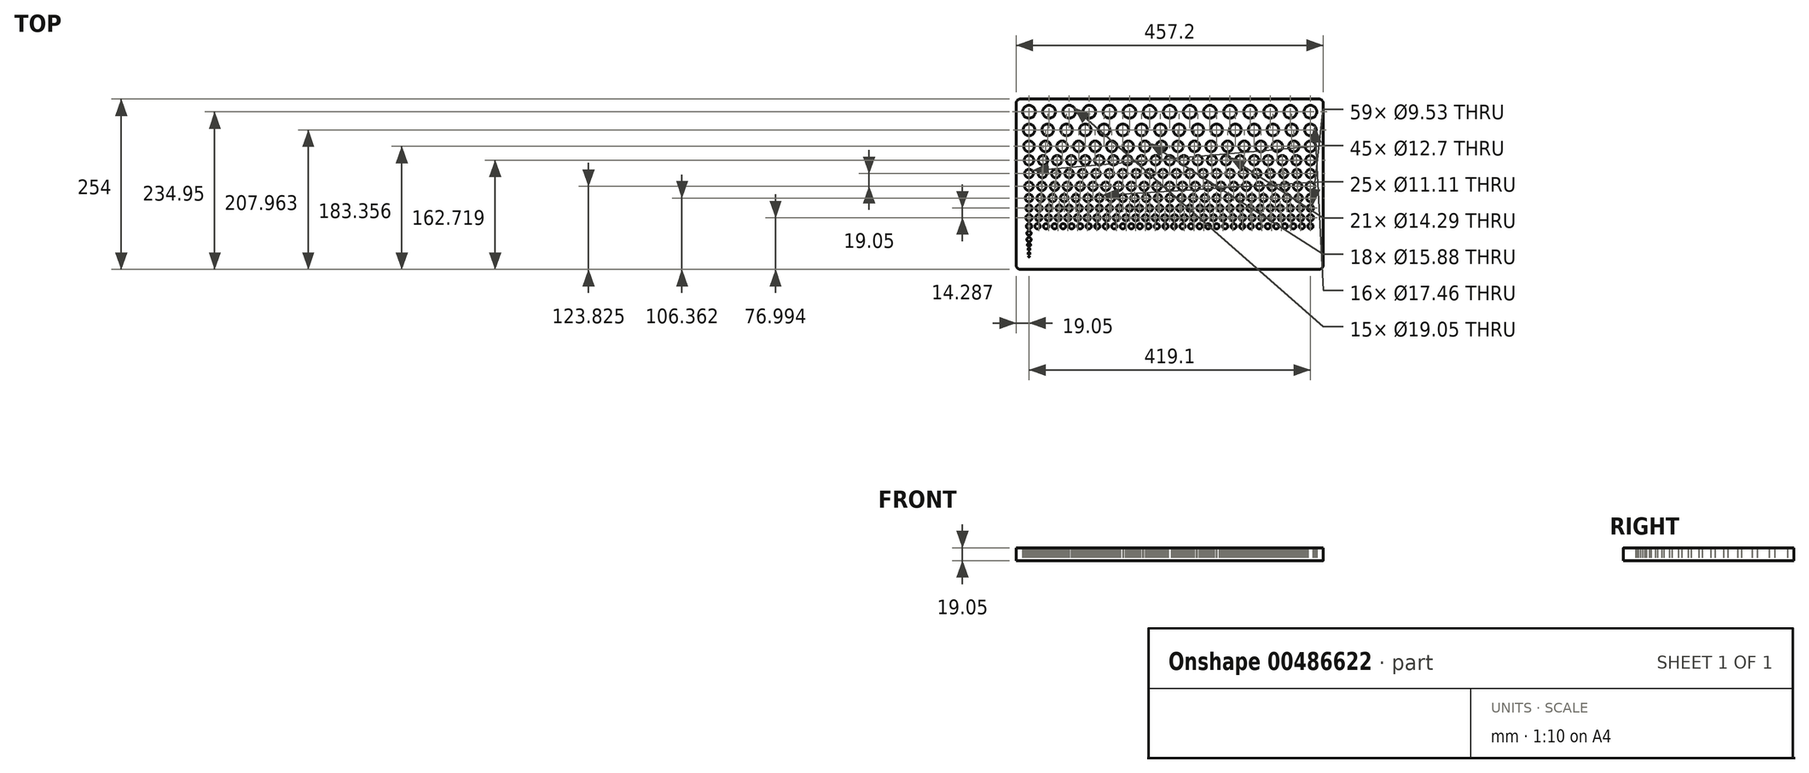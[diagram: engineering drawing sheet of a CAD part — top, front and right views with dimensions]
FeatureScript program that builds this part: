
annotation { "Feature Type Name" : "Feature", "Feature Type Description" : "" }
export const myFeature = defineFeature(function(context is Context, id is Id, definition is map)
    precondition{}
    {
        {
            var Q0;
            Q0=qCreatedBy(makeId("Top.planeOp"),FACE);
            var sketch = newSketch(context, id + "F0", { "sketchPlane" : qUnion([Q0])});
            skLineSegment(sketch, "E0.bottom", {"start": v(6.35, 0) * mm, "end": v(450.85, 0) * mm});
            skLineSegment(sketch, "E0.top", {"start": v(6.35, 254) * mm, "end": v(450.85, 254) * mm});
            skLineSegment(sketch, "E0.left", {"start": v(0, 6.35) * mm, "end": v(0, 247.65) * mm});
            skLineSegment(sketch, "E0.right", {"start": v(457.2, 6.35) * mm, "end": v(457.2, 247.65) * mm});
            skPoint(sketch, "E1.visualSharp", {"position": v(0, 254) * mm});
            skArc(sketch, "E1.filletArc", {"start": v(6.35, 254) * mm, "mid": v(1.86, 252.14) * mm, "end": v(0, 247.65) * mm});
            skPoint(sketch, "E2.visualSharp", {"position": v(457.2, 254) * mm});
            skArc(sketch, "E2.filletArc", {"start": v(457.2, 247.65) * mm, "mid": v(455.34, 252.14) * mm, "end": v(450.85, 254) * mm});
            skPoint(sketch, "E3.visualSharp", {"position": v(457.2, 0) * mm});
            skArc(sketch, "E3.filletArc", {"start": v(450.85, 0) * mm, "mid": v(455.34, 1.86) * mm, "end": v(457.2, 6.35) * mm});
            skPoint(sketch, "E4.visualSharp", {"position": v(0, 0) * mm});
            skArc(sketch, "E4.filletArc", {"start": v(0, 6.35) * mm, "mid": v(1.86, 1.86) * mm, "end": v(6.35, 0) * mm});
            skLineSegment(sketch, "E5", {"start": v(19.05, 234.95) * mm, "end": v(438.15, 234.95) * mm, "construction": true});
            skPoint(sketch, "E6", {"position": v(19.05, 234.95) * mm});
            skCircle(sketch, "E7", {"center": v(19.05, 234.95) * mm, "radius": 9.53 * mm});
            skLineSegment(sketch, "E8", {"start": v(19.05, 234.95) * mm, "end": v(19.05, 19.05) * mm, "construction": true});
            skCircle(sketch, "E9", {"center": v(19.05, 207.96) * mm, "radius": 8.73 * mm});
            skCircle(sketch, "E10.1.0.0", {"center": v(48.99, 234.95) * mm, "radius": 9.53 * mm});
            skCircle(sketch, "E10.2.0.0", {"center": v(78.92, 234.95) * mm, "radius": 9.53 * mm});
            skCircle(sketch, "E10.3.0.0", {"center": v(108.86, 234.95) * mm, "radius": 9.53 * mm});
            skCircle(sketch, "E10.4.0.0", {"center": v(138.8, 234.95) * mm, "radius": 9.53 * mm});
            skCircle(sketch, "E10.5.0.0", {"center": v(168.73, 234.95) * mm, "radius": 9.53 * mm});
            skCircle(sketch, "E10.6.0.0", {"center": v(198.66, 234.95) * mm, "radius": 9.53 * mm});
            skCircle(sketch, "E10.7.0.0", {"center": v(228.6, 234.95) * mm, "radius": 9.53 * mm});
            skCircle(sketch, "E10.8.0.0", {"center": v(258.54, 234.95) * mm, "radius": 9.53 * mm});
            skCircle(sketch, "E10.9.0.0", {"center": v(288.47, 234.95) * mm, "radius": 9.53 * mm});
            skCircle(sketch, "E10.10.0.0", {"center": v(318.4, 234.95) * mm, "radius": 9.53 * mm});
            skCircle(sketch, "E10.11.0.0", {"center": v(348.34, 234.95) * mm, "radius": 9.53 * mm});
            skCircle(sketch, "E10.12.0.0", {"center": v(378.28, 234.95) * mm, "radius": 9.53 * mm});
            skCircle(sketch, "E10.13.0.0", {"center": v(408.21, 234.95) * mm, "radius": 9.53 * mm});
            skCircle(sketch, "E10.14.0.0", {"center": v(438.15, 234.95) * mm, "radius": 9.53 * mm});
            skLineSegment(sketch, "E10.direction1", {"start": v(19.05, 234.95) * mm, "end": v(48.99, 234.95) * mm, "construction": true});
            skCircle(sketch, "E11", {"center": v(19.05, 183.36) * mm, "radius": 7.94 * mm});
            skCircle(sketch, "E12", {"center": v(19.05, 162.72) * mm, "radius": 7.14 * mm});
            skCircle(sketch, "E13", {"center": v(19.05, 142.88) * mm, "radius": 6.35 * mm});
            skCircle(sketch, "E14", {"center": v(19.05, 123.83) * mm, "radius": 6.35 * mm});
            skCircle(sketch, "E15", {"center": v(19.05, 106.36) * mm, "radius": 5.56 * mm});
            skCircle(sketch, "E16", {"center": v(19.05, 91.28) * mm, "radius": 4.76 * mm});
            skCircle(sketch, "E17", {"center": v(19.05, 77) * mm, "radius": 4.76 * mm});
            skCircle(sketch, "E18", {"center": v(19.05, 64.3) * mm, "radius": 3.97 * mm});
            skCircle(sketch, "E19", {"center": v(19.05, 53.97) * mm, "radius": 3.18 * mm});
            skCircle(sketch, "E20", {"center": v(19.05, 44.45) * mm, "radius": 3.18 * mm});
            skCircle(sketch, "E21", {"center": v(19.05, 36.51) * mm, "radius": 2.38 * mm});
            skCircle(sketch, "E22", {"center": v(19.05, 30.16) * mm, "radius": 1.59 * mm});
            skCircle(sketch, "E23", {"center": v(19.05, 23.81) * mm, "radius": 1.59 * mm});
            skCircle(sketch, "E24", {"center": v(19.05, 19.05) * mm, "radius": 0.8 * mm});
            skCircle(sketch, "E25.1.0.0", {"center": v(47, 207.96) * mm, "radius": 8.73 * mm});
            skCircle(sketch, "E25.2.0.0", {"center": v(74.93, 207.96) * mm, "radius": 8.73 * mm});
            skCircle(sketch, "E25.3.0.0", {"center": v(102.87, 207.96) * mm, "radius": 8.73 * mm});
            skCircle(sketch, "E25.4.0.0", {"center": v(130.81, 207.96) * mm, "radius": 8.73 * mm});
            skCircle(sketch, "E25.5.0.0", {"center": v(158.75, 207.96) * mm, "radius": 8.73 * mm});
            skCircle(sketch, "E25.6.0.0", {"center": v(186.7, 207.96) * mm, "radius": 8.73 * mm});
            skCircle(sketch, "E25.7.0.0", {"center": v(214.63, 207.96) * mm, "radius": 8.73 * mm});
            skCircle(sketch, "E25.8.0.0", {"center": v(242.57, 207.96) * mm, "radius": 8.73 * mm});
            skCircle(sketch, "E25.9.0.0", {"center": v(270.51, 207.96) * mm, "radius": 8.73 * mm});
            skCircle(sketch, "E25.10.0.0", {"center": v(298.45, 207.96) * mm, "radius": 8.73 * mm});
            skCircle(sketch, "E25.11.0.0", {"center": v(326.4, 207.96) * mm, "radius": 8.73 * mm});
            skCircle(sketch, "E25.12.0.0", {"center": v(354.33, 207.96) * mm, "radius": 8.73 * mm});
            skCircle(sketch, "E25.13.0.0", {"center": v(382.27, 207.96) * mm, "radius": 8.73 * mm});
            skCircle(sketch, "E25.14.0.0", {"center": v(410.21, 207.96) * mm, "radius": 8.73 * mm});
            skCircle(sketch, "E25.15.0.0", {"center": v(438.15, 207.96) * mm, "radius": 8.73 * mm});
            skLineSegment(sketch, "E25.direction1", {"start": v(19.05, 207.96) * mm, "end": v(47, 207.96) * mm, "construction": true});
            skCircle(sketch, "E26.1.0.0", {"center": v(43.7, 183.36) * mm, "radius": 7.94 * mm});
            skCircle(sketch, "E26.2.0.0", {"center": v(68.36, 183.36) * mm, "radius": 7.94 * mm});
            skCircle(sketch, "E26.3.0.0", {"center": v(93, 183.36) * mm, "radius": 7.94 * mm});
            skCircle(sketch, "E26.4.0.0", {"center": v(117.66, 183.36) * mm, "radius": 7.94 * mm});
            skCircle(sketch, "E26.5.0.0", {"center": v(142.31, 183.36) * mm, "radius": 7.94 * mm});
            skCircle(sketch, "E26.6.0.0", {"center": v(166.97, 183.36) * mm, "radius": 7.94 * mm});
            skCircle(sketch, "E26.7.0.0", {"center": v(191.62, 183.36) * mm, "radius": 7.94 * mm});
            skCircle(sketch, "E26.8.0.0", {"center": v(216.27, 183.36) * mm, "radius": 7.94 * mm});
            skCircle(sketch, "E26.9.0.0", {"center": v(240.93, 183.36) * mm, "radius": 7.94 * mm});
            skCircle(sketch, "E26.10.0.0", {"center": v(265.58, 183.36) * mm, "radius": 7.94 * mm});
            skCircle(sketch, "E26.11.0.0", {"center": v(290.23, 183.36) * mm, "radius": 7.94 * mm});
            skCircle(sketch, "E26.12.0.0", {"center": v(314.89, 183.36) * mm, "radius": 7.94 * mm});
            skCircle(sketch, "E26.13.0.0", {"center": v(339.54, 183.36) * mm, "radius": 7.94 * mm});
            skCircle(sketch, "E26.14.0.0", {"center": v(364.2, 183.36) * mm, "radius": 7.94 * mm});
            skCircle(sketch, "E26.15.0.0", {"center": v(388.84, 183.36) * mm, "radius": 7.94 * mm});
            skCircle(sketch, "E26.16.0.0", {"center": v(413.5, 183.36) * mm, "radius": 7.94 * mm});
            skCircle(sketch, "E26.17.0.0", {"center": v(438.15, 183.36) * mm, "radius": 7.94 * mm});
            skLineSegment(sketch, "E26.direction1", {"start": v(19.05, 183.36) * mm, "end": v(43.7, 183.36) * mm, "construction": true});
            skCircle(sketch, "E27.1.0.0", {"center": v(40, 162.72) * mm, "radius": 7.14 * mm});
            skCircle(sketch, "E27.2.0.0", {"center": v(60.96, 162.72) * mm, "radius": 7.14 * mm});
            skCircle(sketch, "E27.3.0.0", {"center": v(81.92, 162.72) * mm, "radius": 7.14 * mm});
            skCircle(sketch, "E27.4.0.0", {"center": v(102.87, 162.72) * mm, "radius": 7.14 * mm});
            skCircle(sketch, "E27.5.0.0", {"center": v(123.83, 162.72) * mm, "radius": 7.14 * mm});
            skCircle(sketch, "E27.6.0.0", {"center": v(144.78, 162.72) * mm, "radius": 7.14 * mm});
            skCircle(sketch, "E27.7.0.0", {"center": v(165.74, 162.72) * mm, "radius": 7.14 * mm});
            skCircle(sketch, "E27.8.0.0", {"center": v(186.7, 162.72) * mm, "radius": 7.14 * mm});
            skCircle(sketch, "E27.9.0.0", {"center": v(207.65, 162.72) * mm, "radius": 7.14 * mm});
            skCircle(sketch, "E27.10.0.0", {"center": v(228.6, 162.72) * mm, "radius": 7.14 * mm});
            skCircle(sketch, "E27.11.0.0", {"center": v(249.56, 162.72) * mm, "radius": 7.14 * mm});
            skCircle(sketch, "E27.12.0.0", {"center": v(270.51, 162.72) * mm, "radius": 7.14 * mm});
            skCircle(sketch, "E27.13.0.0", {"center": v(291.47, 162.72) * mm, "radius": 7.14 * mm});
            skCircle(sketch, "E27.14.0.0", {"center": v(312.42, 162.72) * mm, "radius": 7.14 * mm});
            skCircle(sketch, "E27.15.0.0", {"center": v(333.38, 162.72) * mm, "radius": 7.14 * mm});
            skCircle(sketch, "E27.16.0.0", {"center": v(354.33, 162.72) * mm, "radius": 7.14 * mm});
            skCircle(sketch, "E27.17.0.0", {"center": v(375.29, 162.72) * mm, "radius": 7.14 * mm});
            skCircle(sketch, "E27.18.0.0", {"center": v(396.24, 162.72) * mm, "radius": 7.14 * mm});
            skCircle(sketch, "E27.19.0.0", {"center": v(417.2, 162.72) * mm, "radius": 7.14 * mm});
            skLineSegment(sketch, "E27.direction1", {"start": v(19.05, 162.72) * mm, "end": v(40, 162.72) * mm, "construction": true});
            skCircle(sketch, "E28.0.20.0", {"center": v(438.15, 162.72) * mm, "radius": 7.14 * mm});
            skCircle(sketch, "E29.1.0.0", {"center": v(39, 142.88) * mm, "radius": 6.35 * mm});
            skCircle(sketch, "E29.2.0.0", {"center": v(58.96, 142.88) * mm, "radius": 6.35 * mm});
            skCircle(sketch, "E29.3.0.0", {"center": v(78.92, 142.88) * mm, "radius": 6.35 * mm});
            skCircle(sketch, "E29.4.0.0", {"center": v(98.88, 142.88) * mm, "radius": 6.35 * mm});
            skCircle(sketch, "E29.5.0.0", {"center": v(118.84, 142.88) * mm, "radius": 6.35 * mm});
            skCircle(sketch, "E29.6.0.0", {"center": v(138.8, 142.88) * mm, "radius": 6.35 * mm});
            skCircle(sketch, "E29.7.0.0", {"center": v(158.75, 142.88) * mm, "radius": 6.35 * mm});
            skCircle(sketch, "E29.8.0.0", {"center": v(178.7, 142.88) * mm, "radius": 6.35 * mm});
            skCircle(sketch, "E29.9.0.0", {"center": v(198.66, 142.88) * mm, "radius": 6.35 * mm});
            skCircle(sketch, "E29.10.0.0", {"center": v(218.62, 142.88) * mm, "radius": 6.35 * mm});
            skCircle(sketch, "E29.11.0.0", {"center": v(238.58, 142.88) * mm, "radius": 6.35 * mm});
            skCircle(sketch, "E29.12.0.0", {"center": v(258.54, 142.88) * mm, "radius": 6.35 * mm});
            skCircle(sketch, "E29.13.0.0", {"center": v(278.5, 142.88) * mm, "radius": 6.35 * mm});
            skCircle(sketch, "E29.14.0.0", {"center": v(298.45, 142.88) * mm, "radius": 6.35 * mm});
            skCircle(sketch, "E29.15.0.0", {"center": v(318.4, 142.88) * mm, "radius": 6.35 * mm});
            skCircle(sketch, "E29.16.0.0", {"center": v(338.36, 142.88) * mm, "radius": 6.35 * mm});
            skCircle(sketch, "E29.17.0.0", {"center": v(358.32, 142.88) * mm, "radius": 6.35 * mm});
            skCircle(sketch, "E29.18.0.0", {"center": v(378.28, 142.88) * mm, "radius": 6.35 * mm});
            skCircle(sketch, "E29.19.0.0", {"center": v(398.24, 142.88) * mm, "radius": 6.35 * mm});
            skCircle(sketch, "E29.20.0.0", {"center": v(418.2, 142.88) * mm, "radius": 6.35 * mm});
            skCircle(sketch, "E29.21.0.0", {"center": v(438.15, 142.88) * mm, "radius": 6.35 * mm});
            skLineSegment(sketch, "E29.direction1", {"start": v(19.05, 142.88) * mm, "end": v(39, 142.88) * mm, "construction": true});
            skCircle(sketch, "E30.1.0.0", {"center": v(38.1, 123.83) * mm, "radius": 6.35 * mm});
            skCircle(sketch, "E30.2.0.0", {"center": v(57.15, 123.83) * mm, "radius": 6.35 * mm});
            skLineSegment(sketch, "E30.direction1", {"start": v(19.05, 123.83) * mm, "end": v(38.1, 123.83) * mm, "construction": true});
            skCircle(sketch, "E31.0.3.0", {"center": v(76.2, 123.83) * mm, "radius": 6.35 * mm});
            skCircle(sketch, "E31.0.4.0", {"center": v(95.25, 123.83) * mm, "radius": 6.35 * mm});
            skCircle(sketch, "E31.0.5.0", {"center": v(114.3, 123.83) * mm, "radius": 6.35 * mm});
            skCircle(sketch, "E31.0.6.0", {"center": v(133.35, 123.83) * mm, "radius": 6.35 * mm});
            skCircle(sketch, "E31.0.7.0", {"center": v(152.4, 123.83) * mm, "radius": 6.35 * mm});
            skCircle(sketch, "E31.0.8.0", {"center": v(171.45, 123.83) * mm, "radius": 6.35 * mm});
            skCircle(sketch, "E31.0.9.0", {"center": v(190.5, 123.83) * mm, "radius": 6.35 * mm});
            skCircle(sketch, "E31.0.10.0", {"center": v(209.55, 123.83) * mm, "radius": 6.35 * mm});
            skCircle(sketch, "E31.0.11.0", {"center": v(228.6, 123.83) * mm, "radius": 6.35 * mm});
            skCircle(sketch, "E31.0.12.0", {"center": v(247.65, 123.83) * mm, "radius": 6.35 * mm});
            skCircle(sketch, "E31.0.13.0", {"center": v(266.7, 123.83) * mm, "radius": 6.35 * mm});
            skCircle(sketch, "E31.0.14.0", {"center": v(285.75, 123.83) * mm, "radius": 6.35 * mm});
            skCircle(sketch, "E31.0.15.0", {"center": v(304.8, 123.83) * mm, "radius": 6.35 * mm});
            skCircle(sketch, "E31.0.16.0", {"center": v(323.85, 123.83) * mm, "radius": 6.35 * mm});
            skCircle(sketch, "E31.0.17.0", {"center": v(342.9, 123.83) * mm, "radius": 6.35 * mm});
            skCircle(sketch, "E31.0.18.0", {"center": v(361.95, 123.83) * mm, "radius": 6.35 * mm});
            skCircle(sketch, "E31.0.19.0", {"center": v(381, 123.83) * mm, "radius": 6.35 * mm});
            skCircle(sketch, "E31.0.20.0", {"center": v(400.05, 123.83) * mm, "radius": 6.35 * mm});
            skCircle(sketch, "E31.0.21.0", {"center": v(419.1, 123.83) * mm, "radius": 6.35 * mm});
            skCircle(sketch, "E31.0.22.0", {"center": v(438.15, 123.83) * mm, "radius": 6.35 * mm});
            skCircle(sketch, "E32.1.0.0", {"center": v(36.51, 106.36) * mm, "radius": 5.56 * mm});
            skCircle(sketch, "E32.2.0.0", {"center": v(53.98, 106.36) * mm, "radius": 5.56 * mm});
            skCircle(sketch, "E32.3.0.0", {"center": v(71.44, 106.36) * mm, "radius": 5.56 * mm});
            skCircle(sketch, "E32.4.0.0", {"center": v(88.9, 106.36) * mm, "radius": 5.56 * mm});
            skCircle(sketch, "E32.5.0.0", {"center": v(106.36, 106.36) * mm, "radius": 5.56 * mm});
            skCircle(sketch, "E32.6.0.0", {"center": v(123.83, 106.36) * mm, "radius": 5.56 * mm});
            skCircle(sketch, "E32.7.0.0", {"center": v(141.29, 106.36) * mm, "radius": 5.56 * mm});
            skCircle(sketch, "E32.8.0.0", {"center": v(158.75, 106.36) * mm, "radius": 5.56 * mm});
            skCircle(sketch, "E32.9.0.0", {"center": v(176.21, 106.36) * mm, "radius": 5.56 * mm});
            skCircle(sketch, "E32.10.0.0", {"center": v(193.68, 106.36) * mm, "radius": 5.56 * mm});
            skCircle(sketch, "E32.11.0.0", {"center": v(211.14, 106.36) * mm, "radius": 5.56 * mm});
            skCircle(sketch, "E32.12.0.0", {"center": v(228.6, 106.36) * mm, "radius": 5.56 * mm});
            skCircle(sketch, "E32.13.0.0", {"center": v(246.06, 106.36) * mm, "radius": 5.56 * mm});
            skCircle(sketch, "E32.14.0.0", {"center": v(263.53, 106.36) * mm, "radius": 5.56 * mm});
            skCircle(sketch, "E32.15.0.0", {"center": v(280.99, 106.36) * mm, "radius": 5.56 * mm});
            skCircle(sketch, "E32.16.0.0", {"center": v(298.45, 106.36) * mm, "radius": 5.56 * mm});
            skCircle(sketch, "E32.17.0.0", {"center": v(315.91, 106.36) * mm, "radius": 5.56 * mm});
            skCircle(sketch, "E32.18.0.0", {"center": v(333.38, 106.36) * mm, "radius": 5.56 * mm});
            skCircle(sketch, "E32.19.0.0", {"center": v(350.84, 106.36) * mm, "radius": 5.56 * mm});
            skCircle(sketch, "E32.20.0.0", {"center": v(368.3, 106.36) * mm, "radius": 5.56 * mm});
            skCircle(sketch, "E32.21.0.0", {"center": v(385.76, 106.36) * mm, "radius": 5.56 * mm});
            skCircle(sketch, "E32.22.0.0", {"center": v(403.23, 106.36) * mm, "radius": 5.56 * mm});
            skCircle(sketch, "E32.23.0.0", {"center": v(420.69, 106.36) * mm, "radius": 5.56 * mm});
            skCircle(sketch, "E32.24.0.0", {"center": v(438.15, 106.36) * mm, "radius": 5.56 * mm});
            skLineSegment(sketch, "E32.direction1", {"start": v(19.05, 106.36) * mm, "end": v(36.51, 106.36) * mm, "construction": true});
            skCircle(sketch, "E33.1.0.0", {"center": v(34.02, 91.28) * mm, "radius": 4.76 * mm});
            skCircle(sketch, "E33.2.0.0", {"center": v(48.99, 91.28) * mm, "radius": 4.76 * mm});
            skCircle(sketch, "E33.3.0.0", {"center": v(63.95, 91.28) * mm, "radius": 4.76 * mm});
            skCircle(sketch, "E33.4.0.0", {"center": v(78.92, 91.28) * mm, "radius": 4.76 * mm});
            skCircle(sketch, "E33.5.0.0", {"center": v(93.89, 91.28) * mm, "radius": 4.76 * mm});
            skCircle(sketch, "E33.6.0.0", {"center": v(108.86, 91.28) * mm, "radius": 4.76 * mm});
            skCircle(sketch, "E33.7.0.0", {"center": v(123.82, 91.28) * mm, "radius": 4.76 * mm});
            skCircle(sketch, "E33.8.0.0", {"center": v(138.8, 91.28) * mm, "radius": 4.76 * mm});
            skCircle(sketch, "E33.9.0.0", {"center": v(153.76, 91.28) * mm, "radius": 4.76 * mm});
            skCircle(sketch, "E33.10.0.0", {"center": v(168.73, 91.28) * mm, "radius": 4.76 * mm});
            skCircle(sketch, "E33.11.0.0", {"center": v(183.7, 91.28) * mm, "radius": 4.76 * mm});
            skCircle(sketch, "E33.12.0.0", {"center": v(198.66, 91.28) * mm, "radius": 4.76 * mm});
            skCircle(sketch, "E33.13.0.0", {"center": v(213.63, 91.28) * mm, "radius": 4.76 * mm});
            skCircle(sketch, "E33.14.0.0", {"center": v(228.6, 91.28) * mm, "radius": 4.76 * mm});
            skCircle(sketch, "E33.15.0.0", {"center": v(243.57, 91.28) * mm, "radius": 4.76 * mm});
            skCircle(sketch, "E33.16.0.0", {"center": v(258.54, 91.28) * mm, "radius": 4.76 * mm});
            skCircle(sketch, "E33.17.0.0", {"center": v(273.5, 91.28) * mm, "radius": 4.76 * mm});
            skCircle(sketch, "E33.18.0.0", {"center": v(288.47, 91.28) * mm, "radius": 4.76 * mm});
            skCircle(sketch, "E33.19.0.0", {"center": v(303.44, 91.28) * mm, "radius": 4.76 * mm});
            skCircle(sketch, "E33.20.0.0", {"center": v(318.4, 91.28) * mm, "radius": 4.76 * mm});
            skCircle(sketch, "E33.21.0.0", {"center": v(333.37, 91.28) * mm, "radius": 4.76 * mm});
            skCircle(sketch, "E33.22.0.0", {"center": v(348.34, 91.28) * mm, "radius": 4.76 * mm});
            skCircle(sketch, "E33.23.0.0", {"center": v(363.31, 91.28) * mm, "radius": 4.76 * mm});
            skCircle(sketch, "E33.24.0.0", {"center": v(378.28, 91.28) * mm, "radius": 4.76 * mm});
            skCircle(sketch, "E33.25.0.0", {"center": v(393.25, 91.28) * mm, "radius": 4.76 * mm});
            skCircle(sketch, "E33.26.0.0", {"center": v(408.21, 91.28) * mm, "radius": 4.76 * mm});
            skCircle(sketch, "E33.27.0.0", {"center": v(423.18, 91.28) * mm, "radius": 4.76 * mm});
            skCircle(sketch, "E33.28.0.0", {"center": v(438.15, 91.28) * mm, "radius": 4.76 * mm});
            skLineSegment(sketch, "E33.direction1", {"start": v(19.05, 91.28) * mm, "end": v(34.02, 91.28) * mm, "construction": true});
            skCircle(sketch, "E34.1.0.0", {"center": v(33.5, 77) * mm, "radius": 4.76 * mm});
            skCircle(sketch, "E34.2.0.0", {"center": v(47.95, 77) * mm, "radius": 4.76 * mm});
            skCircle(sketch, "E34.3.0.0", {"center": v(62.4, 77) * mm, "radius": 4.76 * mm});
            skCircle(sketch, "E34.4.0.0", {"center": v(76.86, 77) * mm, "radius": 4.76 * mm});
            skCircle(sketch, "E34.5.0.0", {"center": v(91.3, 77) * mm, "radius": 4.76 * mm});
            skCircle(sketch, "E34.6.0.0", {"center": v(105.76, 77) * mm, "radius": 4.76 * mm});
            skCircle(sketch, "E34.7.0.0", {"center": v(120.21, 77) * mm, "radius": 4.76 * mm});
            skCircle(sketch, "E34.8.0.0", {"center": v(134.66, 77) * mm, "radius": 4.76 * mm});
            skCircle(sketch, "E34.9.0.0", {"center": v(149.12, 77) * mm, "radius": 4.76 * mm});
            skCircle(sketch, "E34.10.0.0", {"center": v(163.57, 77) * mm, "radius": 4.76 * mm});
            skCircle(sketch, "E34.11.0.0", {"center": v(178.02, 77) * mm, "radius": 4.76 * mm});
            skCircle(sketch, "E34.12.0.0", {"center": v(192.47, 77) * mm, "radius": 4.76 * mm});
            skCircle(sketch, "E34.13.0.0", {"center": v(206.92, 77) * mm, "radius": 4.76 * mm});
            skCircle(sketch, "E34.14.0.0", {"center": v(221.37, 77) * mm, "radius": 4.76 * mm});
            skCircle(sketch, "E34.15.0.0", {"center": v(235.83, 77) * mm, "radius": 4.76 * mm});
            skCircle(sketch, "E34.16.0.0", {"center": v(250.28, 77) * mm, "radius": 4.76 * mm});
            skCircle(sketch, "E34.17.0.0", {"center": v(264.73, 77) * mm, "radius": 4.76 * mm});
            skCircle(sketch, "E34.18.0.0", {"center": v(279.18, 77) * mm, "radius": 4.76 * mm});
            skCircle(sketch, "E34.19.0.0", {"center": v(293.63, 77) * mm, "radius": 4.76 * mm});
            skCircle(sketch, "E34.20.0.0", {"center": v(308.08, 77) * mm, "radius": 4.76 * mm});
            skCircle(sketch, "E34.21.0.0", {"center": v(322.54, 77) * mm, "radius": 4.76 * mm});
            skCircle(sketch, "E34.22.0.0", {"center": v(336.99, 77) * mm, "radius": 4.76 * mm});
            skCircle(sketch, "E34.23.0.0", {"center": v(351.44, 77) * mm, "radius": 4.76 * mm});
            skCircle(sketch, "E34.24.0.0", {"center": v(365.9, 77) * mm, "radius": 4.76 * mm});
            skCircle(sketch, "E34.25.0.0", {"center": v(380.34, 77) * mm, "radius": 4.76 * mm});
            skCircle(sketch, "E34.26.0.0", {"center": v(394.8, 77) * mm, "radius": 4.76 * mm});
            skCircle(sketch, "E34.27.0.0", {"center": v(409.25, 77) * mm, "radius": 4.76 * mm});
            skCircle(sketch, "E34.28.0.0", {"center": v(423.7, 77) * mm, "radius": 4.76 * mm});
            skCircle(sketch, "E34.29.0.0", {"center": v(438.15, 77) * mm, "radius": 4.76 * mm});
            skLineSegment(sketch, "E34.direction1", {"start": v(19.05, 77) * mm, "end": v(33.5, 77) * mm, "construction": true});
            skCircle(sketch, "E35.1.0.0", {"center": v(31.75, 64.3) * mm, "radius": 3.97 * mm});
            skCircle(sketch, "E35.2.0.0", {"center": v(44.45, 64.3) * mm, "radius": 3.97 * mm});
            skCircle(sketch, "E35.3.0.0", {"center": v(57.15, 64.3) * mm, "radius": 3.97 * mm});
            skCircle(sketch, "E35.4.0.0", {"center": v(69.85, 64.3) * mm, "radius": 3.97 * mm});
            skCircle(sketch, "E35.5.0.0", {"center": v(82.55, 64.3) * mm, "radius": 3.97 * mm});
            skCircle(sketch, "E35.6.0.0", {"center": v(95.25, 64.3) * mm, "radius": 3.97 * mm});
            skCircle(sketch, "E35.7.0.0", {"center": v(107.95, 64.3) * mm, "radius": 3.97 * mm});
            skCircle(sketch, "E35.8.0.0", {"center": v(120.65, 64.3) * mm, "radius": 3.97 * mm});
            skCircle(sketch, "E35.9.0.0", {"center": v(133.35, 64.3) * mm, "radius": 3.97 * mm});
            skCircle(sketch, "E35.10.0.0", {"center": v(146.05, 64.3) * mm, "radius": 3.97 * mm});
            skCircle(sketch, "E35.11.0.0", {"center": v(158.75, 64.3) * mm, "radius": 3.97 * mm});
            skCircle(sketch, "E35.12.0.0", {"center": v(171.45, 64.3) * mm, "radius": 3.97 * mm});
            skCircle(sketch, "E35.13.0.0", {"center": v(184.15, 64.3) * mm, "radius": 3.97 * mm});
            skCircle(sketch, "E35.14.0.0", {"center": v(196.85, 64.3) * mm, "radius": 3.97 * mm});
            skCircle(sketch, "E35.15.0.0", {"center": v(209.55, 64.3) * mm, "radius": 3.97 * mm});
            skCircle(sketch, "E35.16.0.0", {"center": v(222.25, 64.3) * mm, "radius": 3.97 * mm});
            skCircle(sketch, "E35.17.0.0", {"center": v(234.95, 64.3) * mm, "radius": 3.97 * mm});
            skCircle(sketch, "E35.18.0.0", {"center": v(247.65, 64.3) * mm, "radius": 3.97 * mm});
            skCircle(sketch, "E35.19.0.0", {"center": v(260.35, 64.3) * mm, "radius": 3.97 * mm});
            skCircle(sketch, "E35.20.0.0", {"center": v(273.05, 64.3) * mm, "radius": 3.97 * mm});
            skCircle(sketch, "E35.21.0.0", {"center": v(285.75, 64.3) * mm, "radius": 3.97 * mm});
            skCircle(sketch, "E35.22.0.0", {"center": v(298.45, 64.3) * mm, "radius": 3.97 * mm});
            skCircle(sketch, "E35.23.0.0", {"center": v(311.15, 64.3) * mm, "radius": 3.97 * mm});
            skCircle(sketch, "E35.24.0.0", {"center": v(323.85, 64.3) * mm, "radius": 3.97 * mm});
            skCircle(sketch, "E35.25.0.0", {"center": v(336.55, 64.3) * mm, "radius": 3.97 * mm});
            skCircle(sketch, "E35.26.0.0", {"center": v(349.25, 64.3) * mm, "radius": 3.97 * mm});
            skCircle(sketch, "E35.27.0.0", {"center": v(361.95, 64.3) * mm, "radius": 3.97 * mm});
            skCircle(sketch, "E35.28.0.0", {"center": v(374.65, 64.3) * mm, "radius": 3.97 * mm});
            skCircle(sketch, "E35.29.0.0", {"center": v(387.35, 64.3) * mm, "radius": 3.97 * mm});
            skCircle(sketch, "E35.30.0.0", {"center": v(400.05, 64.3) * mm, "radius": 3.97 * mm});
            skCircle(sketch, "E35.31.0.0", {"center": v(412.75, 64.3) * mm, "radius": 3.97 * mm});
            skCircle(sketch, "E35.32.0.0", {"center": v(425.45, 64.3) * mm, "radius": 3.97 * mm});
            skLineSegment(sketch, "E35.direction1", {"start": v(19.05, 64.3) * mm, "end": v(31.75, 64.3) * mm, "construction": true});
            skCircle(sketch, "E36.0.33.0", {"center": v(438.15, 64.3) * mm, "radius": 3.97 * mm});
            skSolve(sketch);
        }
        {
            var Q0;
            Q0 = qSketchRegion(id + "F0", true);
            extrude(context, id + "F1", {"entities" : qUnion([Q0]), "depth" : 19.05 * mm});
        }
    });
